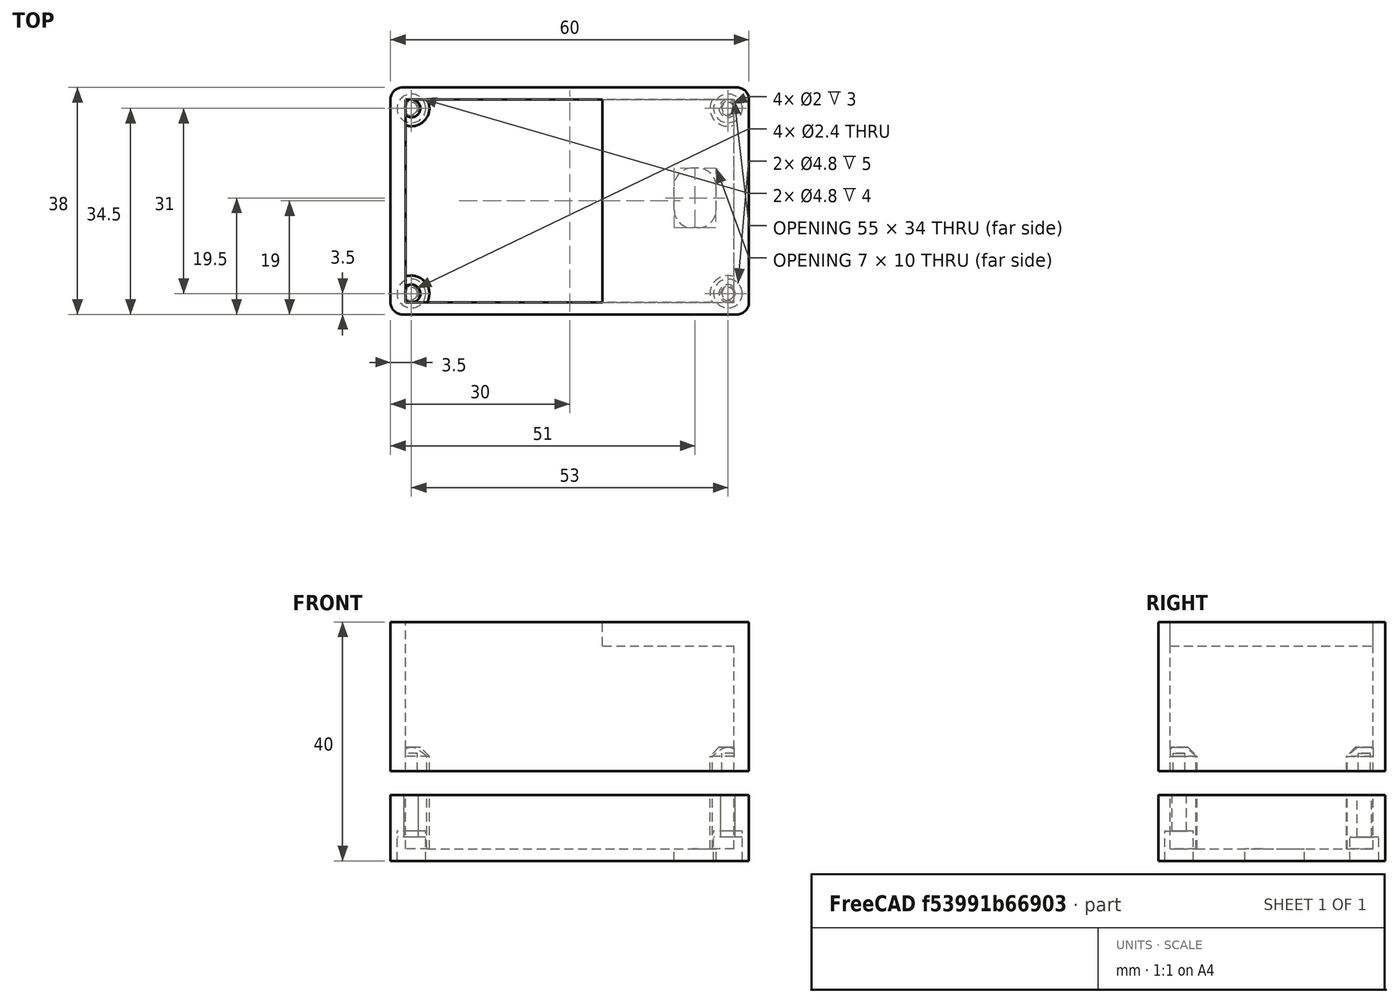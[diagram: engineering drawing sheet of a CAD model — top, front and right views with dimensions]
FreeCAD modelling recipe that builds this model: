
FCSTD DOCUMENT  (FreeCAD 0.18R16093 +53 (Git))
Label: caja_alerta_matrixLED
License: All rights reserved
LicenseURL: http://en.wikipedia.org/wiki/All_rights_reserved
objects: Part::Cylinder×20, Part::MultiFuse×10, Part::Box×6, Part::Cut×5, Part::Chamfer×4, Part::Fillet×3
note: 48 computed .brp shape members not serialized (recipe doc carries the construction recipe); baked Part::Feature solids carry a one-line shape summary decoded from their .brp

FEATURE [Part::Box] Box  label="Cube"
  AttacherType = Attacher::AttachEngine3D
  Height = 25
  Length = 60
  Placement = pos=(-0.5,-0.5,0) rot=(0,0,1;0rad)
  Width = 38
FEATURE [Part::Box] Box001  label="vaciado"
  AttacherType = Attacher::AttachEngine3D
  Height = 21
  Length = 55
  Placement = pos=(2,1.5,0) rot=(0,0,1;0rad)
  Width = 34
FEATURE [Part::Box] Box002  label="vaciado001"
  AttacherType = Attacher::AttachEngine3D
  Height = 11
  Length = 33
  Placement = pos=(2,1.5,15) rot=(0,0,1;0rad)
  Width = 34
FEATURE [Part::MultiFuse] Fusion
  Refine = true
  Shapes = -> [Box001,Box002]
FEATURE [Part::Cut] Cut
  Base = -> Box
  Refine = true
  Tool = -> Fusion
FEATURE [Part::Fillet] Fillet
  Base = -> Cut
  Edges = 4 edges r=2: [Edge1,Edge3,Edge6,Edge15]
FEATURE [Part::Box] Box003  label="tapa"
  AttacherType = Attacher::AttachEngine3D
  Height = 11
  Length = 60
  Placement = pos=(-0.5,-0.5,-15) rot=(0,0,1;0rad)
  Width = 38
FEATURE [Part::Box] Box004  label="vaciado tapa"
  AttacherType = Attacher::AttachEngine3D
  Height = 11
  Length = 55
  Placement = pos=(2,1.5,-13) rot=(0,0,1;0rad)
  Width = 34
FEATURE [Part::Cut] Cut001
  Base = -> Box003
  Refine = true
  Tool = -> Box004
FEATURE [Part::Fillet] Fillet001
  Base = -> Cut001
  Edges = 4 edges r=2: [Edge1,Edge3,Edge6,Edge15]
FEATURE [Part::Cylinder] Cylinder
  Angle = 360
  AttacherType = Attacher::AttachEngine3D
  Height = 4
  Placement = pos=(3,3,-15) rot=(0,0,1;0rad)
  Radius = 3
FEATURE [Part::Chamfer] Chamfer001  label="fijacion1"
  Base = -> Cylinder
  Edges = 1 edges r=1.5: [Edge1]
  Placement = pos=(0,0,15) rot=(0,0,1;0rad)
FEATURE [Part::Cylinder] Cylinder001
  Angle = 360
  AttacherType = Attacher::AttachEngine3D
  Height = 13
  Placement = pos=(3,3,-15) rot=(0,0,1;0rad)
  Radius = 2.4
FEATURE [Part::Cylinder] Cylinder002
  Angle = 360
  AttacherType = Attacher::AttachEngine3D
  Height = 7
  Placement = pos=(3,3,-3) rot=(0,0,1;0rad)
  Radius = 1.2
FEATURE [Part::MultiFuse] Fusion001
  Placement = pos=(0,0,-4) rot=(0,0,1;0rad)
  Refine = true
  Shapes = -> [Cylinder001,Cylinder002]
FEATURE [Part::Cylinder] Cylinder003
  Angle = 360
  AttacherType = Attacher::AttachEngine3D
  Height = 4
  Placement = pos=(3,3,-15) rot=(0,0,1;0rad)
  Radius = 3
FEATURE [Part::Chamfer] Chamfer002  label="fijacion002"
  Base = -> Cylinder003
  Edges = 1 edges r=1.5: [Edge1]
  Placement = pos=(53,0,15) rot=(0,0,1;0rad)
FEATURE [Part::Cylinder] Cylinder004
  Angle = 360
  AttacherType = Attacher::AttachEngine3D
  Height = 4
  Placement = pos=(3,3,-15) rot=(0,0,1;0rad)
  Radius = 3
FEATURE [Part::Chamfer] Chamfer003  label="fijacion003"
  Base = -> Cylinder004
  Edges = 1 edges r=1.5: [Edge1]
  Placement = pos=(0,31,15) rot=(0,0,1;0rad)
FEATURE [Part::Cylinder] Cylinder005
  Angle = 360
  AttacherType = Attacher::AttachEngine3D
  Height = 4
  Placement = pos=(3,3,-15) rot=(0,0,1;0rad)
  Radius = 3
FEATURE [Part::Chamfer] Chamfer004  label="fijacion004"
  Base = -> Cylinder005
  Edges = 1 edges r=1.5: [Edge1]
  Placement = pos=(53,31,15) rot=(0,0,1;0rad)
FEATURE [Part::Cylinder] Cylinder006
  Angle = 360
  AttacherType = Attacher::AttachEngine3D
  Height = 13
  Placement = pos=(3,3,-15) rot=(0,0,1;0rad)
  Radius = 2.4
FEATURE [Part::Cylinder] Cylinder007
  Angle = 360
  AttacherType = Attacher::AttachEngine3D
  Height = 7
  Placement = pos=(3,3,-3) rot=(0,0,1;0rad)
  Radius = 1.2
FEATURE [Part::MultiFuse] Fusion003
  Placement = pos=(53,0,-4) rot=(0,0,1;0rad)
  Refine = true
  Shapes = -> [Cylinder006,Cylinder007]
FEATURE [Part::Cylinder] Cylinder008
  Angle = 360
  AttacherType = Attacher::AttachEngine3D
  Height = 12
  Placement = pos=(3,3,-15) rot=(0,0,1;0rad)
  Radius = 2.4
FEATURE [Part::Cylinder] Cylinder009
  Angle = 360
  AttacherType = Attacher::AttachEngine3D
  Height = 7
  Placement = pos=(3,3,-3) rot=(0,0,1;0rad)
  Radius = 1.2
FEATURE [Part::MultiFuse] Fusion004
  Placement = pos=(53,31,-4) rot=(0,0,1;0rad)
  Refine = true
  Shapes = -> [Cylinder008,Cylinder009]
FEATURE [Part::Cylinder] Cylinder010
  Angle = 360
  AttacherType = Attacher::AttachEngine3D
  Height = 12
  Placement = pos=(3,3,-15) rot=(0,0,1;0rad)
  Radius = 2.4
FEATURE [Part::Cylinder] Cylinder011
  Angle = 360
  AttacherType = Attacher::AttachEngine3D
  Height = 7
  Placement = pos=(3,3,-3) rot=(0,0,1;0rad)
  Radius = 1.2
FEATURE [Part::MultiFuse] Fusion005
  Placement = pos=(0,31,-4) rot=(0,0,1;0rad)
  Refine = true
  Shapes = -> [Cylinder010,Cylinder011]
FEATURE [Part::Cylinder] Cylinder012
  Angle = 360
  AttacherType = Attacher::AttachEngine3D
  Height = 11
  Placement = pos=(3,3,-15) rot=(0,0,1;0rad)
  Radius = 3
FEATURE [Part::Cylinder] Cylinder013
  Angle = 360
  AttacherType = Attacher::AttachEngine3D
  Height = 11
  Placement = pos=(56,3,-15) rot=(0,0,1;0rad)
  Radius = 3
FEATURE [Part::Cylinder] Cylinder014
  Angle = 360
  AttacherType = Attacher::AttachEngine3D
  Height = 11
  Placement = pos=(56,34,-15) rot=(0,0,1;0rad)
  Radius = 3
FEATURE [Part::Cylinder] Cylinder015
  Angle = 360
  AttacherType = Attacher::AttachEngine3D
  Height = 11
  Placement = pos=(3,34,-15) rot=(0,0,1;0rad)
  Radius = 3
FEATURE [Part::MultiFuse] Fusion006
  Refine = true
  Shapes = -> [Cylinder015,Cylinder012,Cylinder014,Cylinder013]
FEATURE [Part::MultiFuse] Fusion007
  Refine = true
  Shapes = -> [Fillet001,Fusion006]
FEATURE [Part::MultiFuse] Fusion008
  Placement = pos=(0,0,-4) rot=(0,0,1;0rad)
  Refine = true
  Shapes = -> [Fusion005,Fusion004,Fusion003,Fusion001]
FEATURE [Part::Cut] Cut002  label="tapa001"
  Base = -> Fusion007
  Refine = true
  Tool = -> Fusion008
FEATURE [Part::MultiFuse] Fusion009  label="base"
  Refine = true
  Shapes = -> [Chamfer004,Chamfer002,Chamfer003,Chamfer001,Fillet]
FEATURE [Part::Box] Box005  label="Cube001"
  AttacherType = Attacher::AttachEngine3D
  Height = 6
  Length = 7
  Placement = pos=(45,10,-17) rot=(0,0,1;0rad)
  Width = 10
FEATURE [Part::Fillet] Fillet002
  Base = -> Box005
  Edges = 4 edges r=3: [Edge1,Edge3,Edge5,Edge7]
  Placement = pos=(2,4,0) rot=(0,0,1;0rad)
FEATURE [Part::Cut] Cut003  label="trasera"
  Base = -> Cut002
  Refine = true
  Tool = -> Fillet002
FEATURE [Part::Cylinder] Cylinder016
  Angle = 360
  AttacherType = Attacher::AttachEngine3D
  Height = 3
  Placement = pos=(3,3,0) rot=(0,0,1;0rad)
  Radius = 1
FEATURE [Part::Cylinder] Cylinder017
  Angle = 360
  AttacherType = Attacher::AttachEngine3D
  Height = 3
  Placement = pos=(56,3,0) rot=(0,0,1;0rad)
  Radius = 1
FEATURE [Part::Cylinder] Cylinder018
  Angle = 360
  AttacherType = Attacher::AttachEngine3D
  Height = 3
  Placement = pos=(56,34,0) rot=(0,0,1;0rad)
  Radius = 1
FEATURE [Part::Cylinder] Cylinder019
  Angle = 360
  AttacherType = Attacher::AttachEngine3D
  Height = 3
  Placement = pos=(3,34,0) rot=(0,0,1;0rad)
  Radius = 1
FEATURE [Part::MultiFuse] Fusion010  label="vaciado tornillos caja"
  Refine = true
  Shapes = -> [Cylinder016,Cylinder018,Cylinder019,Cylinder017]
FEATURE [Part::Cut] Cut005  label="frontal"
  Base = -> Fusion009
  Refine = true
  Tool = -> Fusion010
